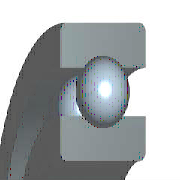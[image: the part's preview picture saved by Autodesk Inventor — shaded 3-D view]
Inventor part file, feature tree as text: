
AUTODESK INVENTOR PART (.ipt)
format: ipt  version: 2025 (Build 290162000, 162)  size: 261,120 bytes
history: native  units: mm (DEFAULTED — no unit token found)
features: other x1, pattern_circular x1
ambient origin geometry x8: Origin, YZ Plane, XZ Plane, XY Plane, X Axis, Y Axis, Z Axis, Center Point
bodies: Solid1 (feature_tree)
feature tree (2):
  other  "轴承体"
  pattern_circular  "IDS_ARRAYBALL[SIMPL:T]"  Angle=90.0deg  [1 undecoded]
note: 1 required parameter value undecoded (feature->parameter linkage not recoverable at this tier; creation-order binding heuristic only, values carry confidence <= 0.55)
